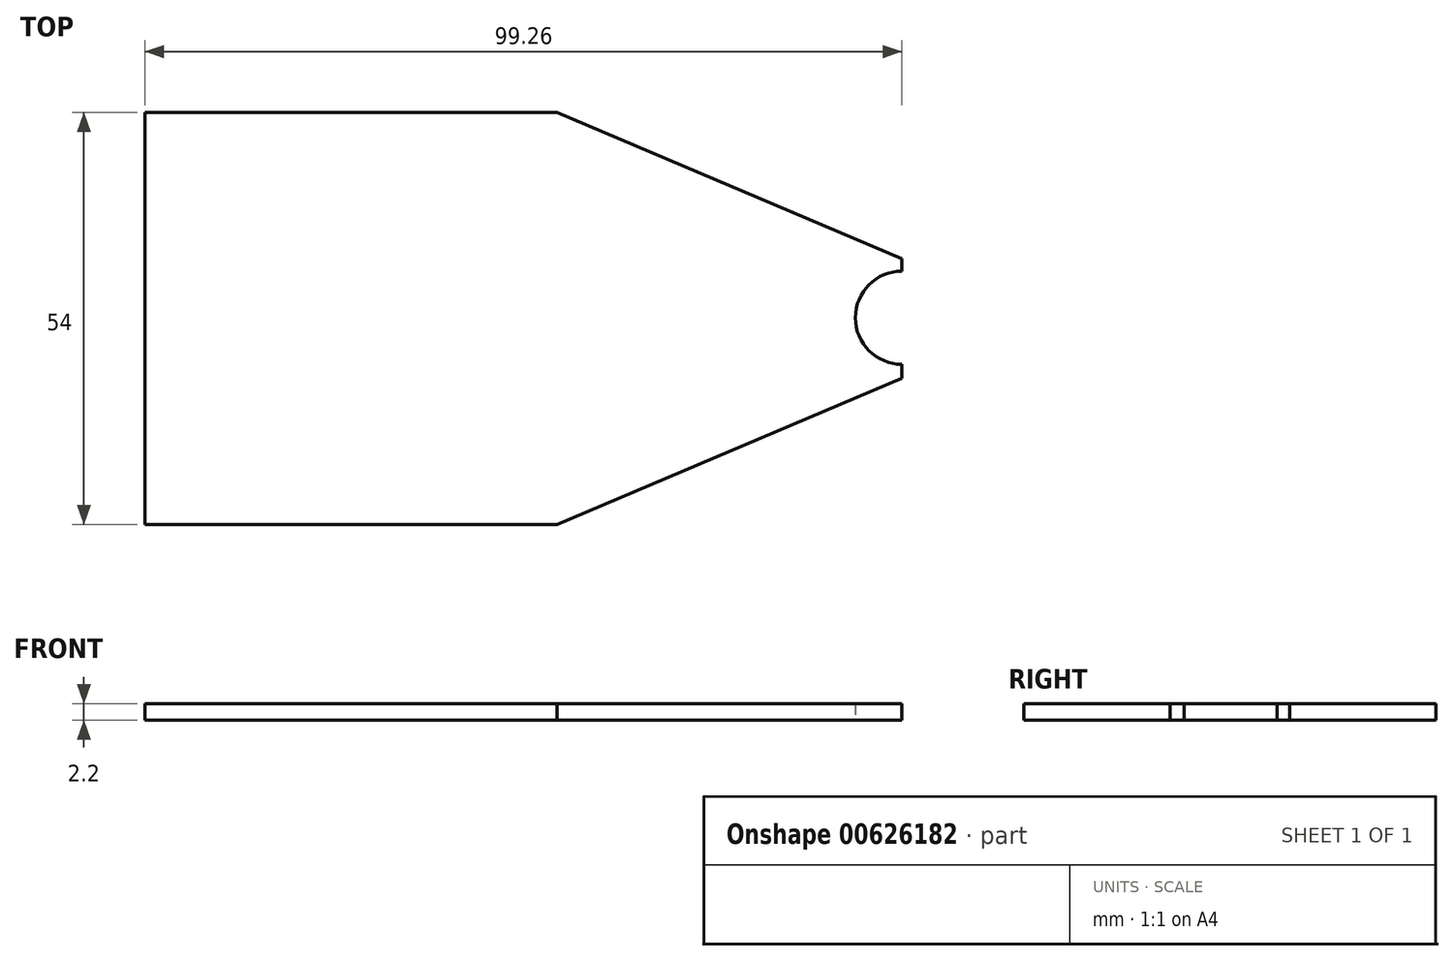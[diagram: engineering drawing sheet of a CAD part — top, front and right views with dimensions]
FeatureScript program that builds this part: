
annotation { "Feature Type Name" : "Feature", "Feature Type Description" : "" }
export const myFeature = defineFeature(function(context is Context, id is Id, definition is map)
    precondition{}
    {
        {
            var Q0;
            Q0=qCreatedBy(makeId("Top.planeOp"),FACE);
            var sketch = newSketch(context, id + "F0", { "sketchPlane" : qUnion([Q0])});
            skLineSegment(sketch, "E0", {"start": v(-33.37, 19.06) * mm, "end": v(11.9, -0.1) * mm});
            skLineSegment(sketch, "E1", {"start": v(-33.37, -34.94) * mm, "end": v(11.9, -15.77) * mm});
            skLineSegment(sketch, "E2.0", {"start": v(-31.37, 16.04) * mm, "end": v(11.9, -2.28) * mm});
            skLineSegment(sketch, "E2.1", {"start": v(-31.37, -7.94) * mm, "end": v(-31.37, 16.04) * mm});
            skLineSegment(sketch, "E2.2", {"start": v(-31.37, -7.94) * mm, "end": v(-31.37, -31.92) * mm});
            skLineSegment(sketch, "E2.3", {"start": v(-31.37, -31.92) * mm, "end": v(11.9, -13.6) * mm});
            skLineSegment(sketch, "E3", {"start": v(-33.37, 19.06) * mm, "end": v(-33.37, -34.94) * mm});
            skLineSegment(sketch, "E4", {"start": v(-31.37, 16.04) * mm, "end": v(-33.37, 16.89) * mm});
            skLineSegment(sketch, "E5", {"start": v(-31.37, -31.92) * mm, "end": v(-33.37, -32.77) * mm});
            skLineSegment(sketch, "E6.bottom", {"start": v(-33.37, -34.94) * mm, "end": v(-87.37, -34.94) * mm});
            skLineSegment(sketch, "E6.top", {"start": v(-33.37, 19.06) * mm, "end": v(-87.37, 19.06) * mm});
            skLineSegment(sketch, "E6.left", {"start": v(-33.37, -34.94) * mm, "end": v(-33.37, 19.06) * mm});
            skLineSegment(sketch, "E6.right", {"start": v(-87.37, -34.94) * mm, "end": v(-87.37, 19.06) * mm});
            skArc(sketch, "E7", {"start": v(11.9, -1.74) * mm, "mid": v(5.8, -7.84) * mm, "end": v(11.9, -13.94) * mm});
            skLineSegment(sketch, "E8", {"start": v(11.9, -7.94) * mm, "end": v(11.9, 7.54) * mm});
            skLineSegment(sketch, "E9", {"start": v(11.9, 7.54) * mm, "end": v(11.9, -21.3) * mm});
            skSolve(sketch);
        }
        {
            var Q0;
            {var subQ3=sQuery(id+"F0.wireOp",EDGE,"E6.bottom");Q0=makeQuery(id+"F0.imprint","IMPRINT",FACE,{"disambiguationData":[TD([[makeQuery(id+"F0.imprint","IMPRINT",EDGE,{"derivedFrom":subQ3}),-1.0]])]});}
            var Q1;
            {var subQ1=sQuery(id+"F0.wireOp",EDGE,"E0");Q1=makeQuery(id+"F0.imprint","IMPRINT",FACE,{"disambiguationData":[TD([[makeQuery(id+"F0.imprint","IMPRINT",EDGE,{"derivedFrom":subQ1}),-1.0]])]});}
            var Q2;
            Q2=makeQuery(id+"F0.imprint","IMPRINT",FACE,{"disambiguationData":[TD([[makeQuery(id+"F0.imprint","IMPRINT",EDGE,{"derivedFrom":sQuery(id+"F0.wireOp",EDGE,"E2.1")}),1.0]])]});
            var Q3;
            {var subQ6=sQuery(id+"F0.wireOp",EDGE,"E2.1");Q3=makeQuery(id+"F0.imprint","IMPRINT",FACE,{"disambiguationData":[TD([[makeQuery(id+"F0.imprint","IMPRINT",EDGE,{"derivedFrom":subQ6}),-1.0]])]});}
            var Q4;
            {var subQ1=sQuery(id+"F0.wireOp",EDGE,"E1");Q4=makeQuery(id+"F0.imprint","IMPRINT",FACE,{"disambiguationData":[TD([[makeQuery(id+"F0.imprint","IMPRINT",EDGE,{"derivedFrom":subQ1}),1.0]])]});}
            extrude(context, id + "F1", {"entities" : qUnion([Q0, Q1, Q2, Q3, Q4]), "depth" : 2.2 * mm, "offsetDistance" : 25 * mm});
        }
    });
